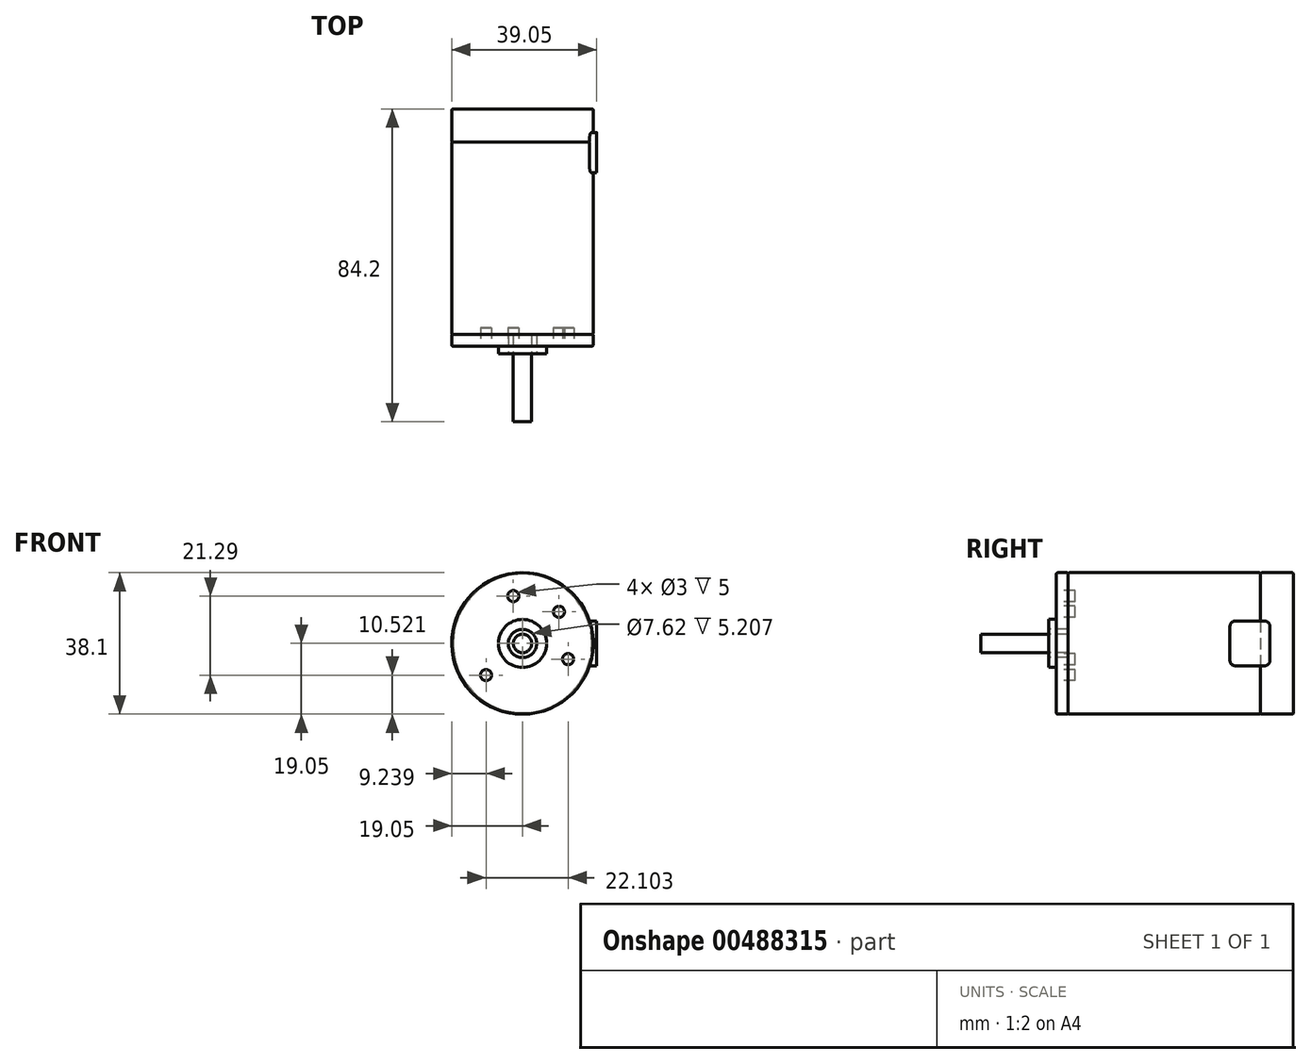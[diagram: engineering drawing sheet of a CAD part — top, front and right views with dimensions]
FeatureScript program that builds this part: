
annotation { "Feature Type Name" : "Feature", "Feature Type Description" : "" }
export const myFeature = defineFeature(function(context is Context, id is Id, definition is map)
    precondition{}
    {
        {
            var Q0;
            Q0=qCreatedBy(makeId("Right.planeOp"),FACE);
            var sketch = newSketch(context, id + "F0", { "sketchPlane" : qUnion([Q0])});
            skLineSegment(sketch, "E0.bottom", {"start": v(20.7, 19.05) * mm, "end": v(23.11, 19.05) * mm});
            skLineSegment(sketch, "E1", {"start": v(23.5, 2.48) * mm, "end": v(0, 2.48) * mm});
            skLineSegment(sketch, "E2", {"start": v(0, 0) * mm, "end": v(23.5, 0) * mm});
            skLineSegment(sketch, "E3", {"start": v(0, 2.48) * mm, "end": v(0, 0) * mm});
            skLineSegment(sketch, "E4", {"start": v(23.5, 18.67) * mm, "end": v(23.5, 0) * mm});
            skArc(sketch, "E5.filletArc", {"start": v(20.7, 19.05) * mm, "mid": v(20.43, 18.94) * mm, "end": v(20.32, 18.67) * mm});
            skPoint(sketch, "E6.visualSharp", {"position": v(23.5, 19.05) * mm});
            skArc(sketch, "E6.filletArc", {"start": v(23.5, 18.67) * mm, "mid": v(23.38, 18.94) * mm, "end": v(23.11, 19.05) * mm});
            skLineSegment(sketch, "E7", {"start": v(77.85, 0) * mm, "end": v(77.85, 4.53) * mm});
            skLineSegment(sketch, "E8", {"start": v(76.35, 6.03) * mm, "end": v(68.56, 6.03) * mm});
            skLineSegment(sketch, "E9", {"start": v(67.06, 4.53) * mm, "end": v(67.06, 0) * mm});
            skPoint(sketch, "E10.visualSharp", {"position": v(67.06, 6.03) * mm});
            skArc(sketch, "E10.filletArc", {"start": v(68.56, 6.03) * mm, "mid": v(67.5, 5.6) * mm, "end": v(67.06, 4.53) * mm});
            skPoint(sketch, "E11.visualSharp", {"position": v(77.85, 6.03) * mm});
            skArc(sketch, "E11.filletArc", {"start": v(77.85, 4.53) * mm, "mid": v(77.41, 5.6) * mm, "end": v(76.35, 6.03) * mm});
            skLineSegment(sketch, "E12.MirrorCS", {"start": v(67.06, -4.53) * mm, "end": v(67.06, 0) * mm});
            skArc(sketch, "E13.MirrorCS", {"start": v(68.56, -6.03) * mm, "mid": v(67.5, -5.6) * mm, "end": v(67.06, -4.53) * mm});
            skLineSegment(sketch, "E14.MirrorCS", {"start": v(76.35, -6.03) * mm, "end": v(68.56, -6.03) * mm});
            skArc(sketch, "E15.MirrorCS", {"start": v(77.85, -4.53) * mm, "mid": v(77.41, -5.6) * mm, "end": v(76.35, -6.03) * mm});
            skLineSegment(sketch, "E16.MirrorCS", {"start": v(77.85, 0) * mm, "end": v(77.85, -4.53) * mm});
            skLineSegment(sketch, "E17", {"start": v(23.5, 3.81) * mm, "end": v(18.29, 3.8) * mm});
            skLineSegment(sketch, "E18", {"start": v(18.29, 3.8) * mm, "end": v(18.29, 6.48) * mm});
            skLineSegment(sketch, "E19", {"start": v(18.29, 6.48) * mm, "end": v(20.32, 6.48) * mm});
            skLineSegment(sketch, "E20", {"start": v(20.32, 6.48) * mm, "end": v(20.32, 18.67) * mm});
            skLineSegment(sketch, "E21", {"start": v(-22.65, 0) * mm, "end": v(114.1, 0) * mm, "construction": true});
            skLineSegment(sketch, "E22", {"start": v(23.88, 19.05) * mm, "end": v(74.93, 19.05) * mm});
            skArc(sketch, "E23", {"start": v(23.88, 19.05) * mm, "mid": v(23.6, 18.94) * mm, "end": v(23.5, 18.67) * mm});
            skArc(sketch, "E24", {"start": v(75.31, 18.67) * mm, "mid": v(75.2, 18.94) * mm, "end": v(74.93, 19.05) * mm});
            skLineSegment(sketch, "E25", {"start": v(75.31, 18.67) * mm, "end": v(75.31, 0) * mm});
            skLineSegment(sketch, "E26", {"start": v(75.7, 19.05) * mm, "end": v(83.82, 19.05) * mm});
            skLineSegment(sketch, "E27", {"start": v(84.2, 18.67) * mm, "end": v(84.2, 0) * mm});
            skArc(sketch, "E28", {"start": v(75.7, 19.05) * mm, "mid": v(75.42, 18.94) * mm, "end": v(75.31, 18.67) * mm});
            skArc(sketch, "E29", {"start": v(84.2, 18.67) * mm, "mid": v(84.09, 18.94) * mm, "end": v(83.82, 19.05) * mm});
            skLineSegment(sketch, "E30", {"start": v(23.5, 0) * mm, "end": v(75.31, 0) * mm});
            skLineSegment(sketch, "E31", {"start": v(75.31, 0) * mm, "end": v(84.2, 0) * mm});
            skSolve(sketch);
        }
        {
            var Q0;
            {var subQ3=sQuery(id+"F0.wireOp",EDGE,"E1");Q0=makeQuery(id+"F0.imprint","IMPRINT",FACE,{"disambiguationData":[TD([[makeQuery(id+"F0.imprint","IMPRINT",EDGE,{"derivedFrom":subQ3}),1.0]])]});}
            var Q1;
            {var subQ4=sQuery(id+"F0.wireOp",EDGE,"aOQpTqtW-oOLi-Vmjm-0HFz-MzQgsTkiUo6G");Q1=makeQuery(id+"F0.imprint","IMPRINT",FACE,{"disambiguationData":[TD([[makeQuery(id+"F0.imprint","IMPRINT",EDGE,{"derivedFrom":subQ4}),1.0]])]});}
            var Q2;
            Q2=makeQuery(id+"F0.imprint","IMPRINT",FACE,{"disambiguationData":[TD([[makeQuery(id+"F0.imprint","IMPRINT",EDGE,{"derivedFrom":sQuery(id+"F0.wireOp",EDGE,"E0.bottom")}),-1.0]])]});
            var Q3;
            {var subQ6=sQuery(id+"F0.wireOp",EDGE,"E7");Q3=makeQuery(id+"F0.imprint","IMPRINT",FACE,{"disambiguationData":[TD([[makeQuery(id+"F0.imprint","IMPRINT",EDGE,{"derivedFrom":subQ6}),1.0]])]});}
            var Q4;
            {var subQ6=sQuery(id+"F0.wireOp",EDGE,"E9");Q4=makeQuery(id+"F0.imprint","IMPRINT",FACE,{"disambiguationData":[TD([[makeQuery(id+"F0.imprint","IMPRINT",EDGE,{"derivedFrom":subQ6}),1.0]])]});}
            var Q5;
            {var subQ6=sQuery(id+"F0.wireOp",EDGE,"E7");Q5=makeQuery(id+"F0.imprint","IMPRINT",FACE,{"disambiguationData":[TD([[makeQuery(id+"F0.imprint","IMPRINT",EDGE,{"derivedFrom":subQ6}),-1.0]])]});}
            var Q6;
            {var subQ2=sQuery(id+"F0.wireOp",EDGE,"E9");Q6=makeQuery(id+"F0.imprint","IMPRINT",FACE,{"disambiguationData":[TD([[makeQuery(id+"F0.imprint","IMPRINT",EDGE,{"derivedFrom":subQ2}),-1.0]])]});}
            var Q7;
            Q7=sQuery(id+"F0.wireOp",EDGE,"E2");
            revolve(context, id + "F1", {"entities" : qUnion([Q0, Q1, Q2, Q3, Q4, Q5, Q6]), "axis" : qUnion([Q7]), "revolveType" : RevolveType.FULL});
        }
        {
            var Q0;
            {var subQ1=sQuery(id+"F0.wireOp",EDGE,"E7");Q0=makeQuery(id+"F0.imprint","IMPRINT",FACE,{"disambiguationData":[TD([[makeQuery(id+"F0.imprint","IMPRINT",EDGE,{"derivedFrom":subQ1}),1.0]])]});}
            var Q1;
            {var subQ0=sQuery(id+"F0.wireOp",EDGE,"E12.MirrorCS");Q1=makeQuery(id+"F0.imprint","IMPRINT",FACE,{"disambiguationData":[TD([[makeQuery(id+"F0.imprint","IMPRINT",EDGE,{"derivedFrom":subQ0}),-1.0]])]});}
            var Q2;
            {var subQ6=sQuery(id+"F0.wireOp",EDGE,"E9");Q2=makeQuery(id+"F0.imprint","IMPRINT",FACE,{"disambiguationData":[TD([[makeQuery(id+"F0.imprint","IMPRINT",EDGE,{"derivedFrom":subQ6}),1.0]])]});}
            extrude(context, id + "F2", {"entities" : qUnion([Q0, Q1, Q2]), "operationType" : NewBodyOperationType.ADD, "depth" : 20 * mm});
        }
        {
            var Q0;
            Q0=makeQuery(id+"F1.opRevolve","SWEPT_FACE",FACE,{"disambiguationData":[OSD([sQuery(id+"F0.wireOp",EDGE,"E20")])]});
            var sketch = newSketch(context, id + "F3", { "sketchPlane" : qUnion([Q0])});
            skCircle(sketch, "E32.0", {"center": v(0, 0) * mm, "radius": 2.48 * mm, "construction": true});
            skLineSegment(sketch, "E33.0", {"start": v(20, 4.53) * mm, "end": v(20, -4.53) * mm, "construction": true});
            skCircle(sketch, "E34", {"center": v(-2.48, 12.76) * mm, "radius": 1.5 * mm});
            skCircle(sketch, "E35", {"center": v(9.81, 8.53) * mm, "radius": 1.5 * mm});
            skCircle(sketch, "E36", {"center": v(12.3, -4.23) * mm, "radius": 1.5 * mm});
            skCircle(sketch, "E37", {"center": v(-9.81, -8.53) * mm, "radius": 1.5 * mm});
            skLineSegment(sketch, "E38", {"start": v(-9.81, -8.53) * mm, "end": v(9.81, 8.53) * mm, "construction": true});
            skCircle(sketch, "E39", {"center": v(0, 0) * mm, "radius": 13 * mm, "construction": true});
            skLineSegment(sketch, "E40", {"start": v(-2.48, 12.76) * mm, "end": v(0, 0) * mm, "construction": true});
            skLineSegment(sketch, "E41", {"start": v(0, 0) * mm, "end": v(12.3, -4.23) * mm, "construction": true});
            skLineSegment(sketch, "E42", {"start": v(-18.68, -19.56) * mm, "end": v(42.49, -19.56) * mm, "construction": true});
            skSolve(sketch);
        }
        {
            var Q0;
            Q0=makeQuery(id+"F3.imprint","IMPRINT",FACE,{"disambiguationData":[TD([[makeQuery(id+"F3.imprint","IMPRINT",EDGE,{"derivedFrom":sQuery(id+"F3.wireOp",EDGE,"E37")}),1.0]])]});
            var Q1;
            Q1=makeQuery(id+"F3.imprint","IMPRINT",FACE,{"disambiguationData":[TD([[makeQuery(id+"F3.imprint","IMPRINT",EDGE,{"derivedFrom":sQuery(id+"F3.wireOp",EDGE,"E34")}),1.0]])]});
            var Q2;
            Q2=makeQuery(id+"F3.imprint","IMPRINT",FACE,{"disambiguationData":[TD([[makeQuery(id+"F3.imprint","IMPRINT",EDGE,{"derivedFrom":sQuery(id+"F3.wireOp",EDGE,"E35")}),1.0]])]});
            var Q3;
            Q3=makeQuery(id+"F3.imprint","IMPRINT",FACE,{"disambiguationData":[TD([[makeQuery(id+"F3.imprint","IMPRINT",EDGE,{"derivedFrom":sQuery(id+"F3.wireOp",EDGE,"E36")}),1.0]])]});
            extrude(context, id + "F4", {"entities" : qUnion([Q0, Q1, Q2, Q3]), "operationType" : NewBodyOperationType.REMOVE, "oppositeDirection" : true, "depth" : 5 * mm});
        }
    });
